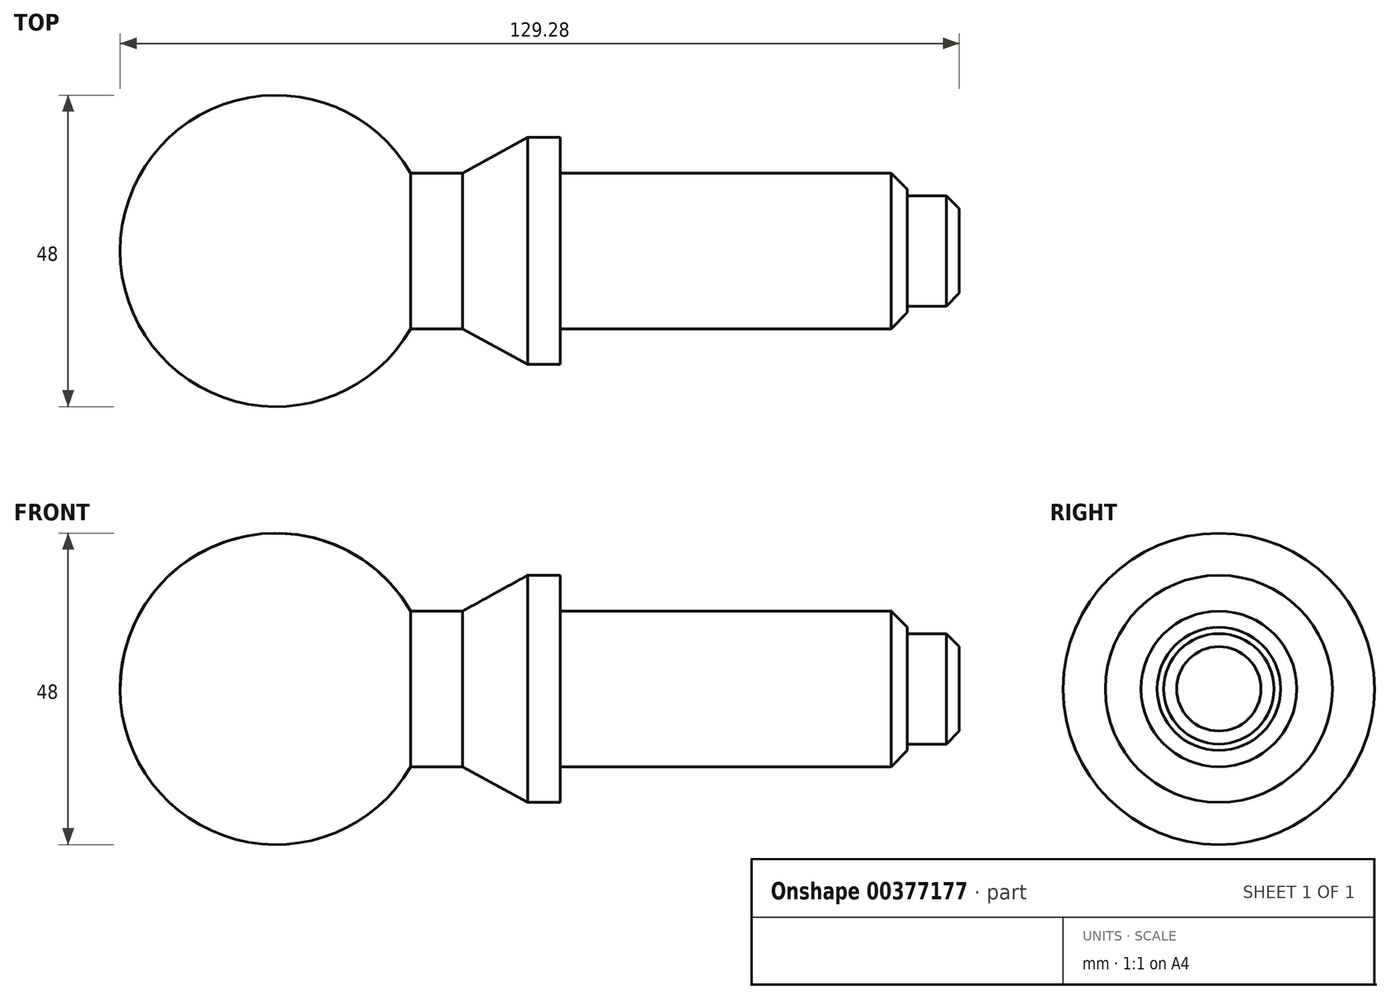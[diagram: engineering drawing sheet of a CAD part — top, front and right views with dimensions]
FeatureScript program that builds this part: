
annotation { "Feature Type Name" : "Feature", "Feature Type Description" : "" }
export const myFeature = defineFeature(function(context is Context, id is Id, definition is map)
    precondition{}
    {
        {
            var Q0;
            Q0=qCreatedBy(makeId("Front.planeOp"),FACE);
            var sketch = newSketch(context, id + "F0", { "sketchPlane" : qUnion([Q0])});
            skLineSegment(sketch, "E0", {"start": v(0, 0) * mm, "end": v(0, 8.5) * mm});
            skLineSegment(sketch, "E1", {"start": v(0, 8.5) * mm, "end": v(-8, 8.5) * mm});
            skLineSegment(sketch, "E2", {"start": v(-8, 8.5) * mm, "end": v(-8, 12) * mm});
            skLineSegment(sketch, "E3", {"start": v(-8, 12) * mm, "end": v(-61.5, 12) * mm});
            skLineSegment(sketch, "E4", {"start": v(-61.5, 12) * mm, "end": v(-61.5, 17.5) * mm});
            skLineSegment(sketch, "E5", {"start": v(-61.5, 17.5) * mm, "end": v(-66.5, 17.5) * mm});
            skLineSegment(sketch, "E6", {"start": v(-66.5, 17.5) * mm, "end": v(-76.5, 12) * mm});
            skLineSegment(sketch, "E7", {"start": v(-76.5, 12) * mm, "end": v(-84.5, 12) * mm});
            skArc(sketch, "E8", {"start": v(-84.5, 12) * mm, "mid": v(-111.5, 23.18) * mm, "end": v(-129.28, 0) * mm});
            skPoint(sketch, "E9.orphan", {"position": v(-84.5, -12) * mm});
            skLineSegment(sketch, "E10", {"start": v(-129.28, 0) * mm, "end": v(0, 0) * mm});
            skSolve(sketch);
        }
        {
            var Q0;
            Q0 = qSketchRegion(id + "F0", true);
            var Q1;
            Q1=sQuery(id+"F0.wireOp",EDGE,"E10");
            revolve(context, id + "F1", {"entities" : qUnion([Q0]), "axis" : qUnion([Q1]), "revolveType" : RevolveType.FULL});
        }
        {
            var Q0;
            Q0=makeQuery(id+"F1.opRevolve","SWEPT_EDGE",EDGE,{"disambiguationData":[OSD([sQuery(id+"F0.wireOp",EDGE,"E0"),sQuery(id+"F0.wireOp",EDGE,"E1")])]});
            chamfer(context, id + "F2", {"entities" : qUnion([Q0]), "chamferType" : ChamferType.OFFSET_ANGLE, "width" : 2 * mm, "oppositeDirection" : false, "angle" : 45 * degree, "tangentPropagation" : true});
        }
        {
            var Q0;
            Q0=makeQuery(id+"F1.opRevolve","SWEPT_EDGE",EDGE,{"disambiguationData":[OSD([sQuery(id+"F0.wireOp",EDGE,"E2"),sQuery(id+"F0.wireOp",EDGE,"E3")])]});
            chamfer(context, id + "F3", {"entities" : qUnion([Q0]), "chamferType" : ChamferType.OFFSET_ANGLE, "width" : 2.5 * mm, "oppositeDirection" : false, "angle" : 45 * degree, "tangentPropagation" : true});
        }
    });
